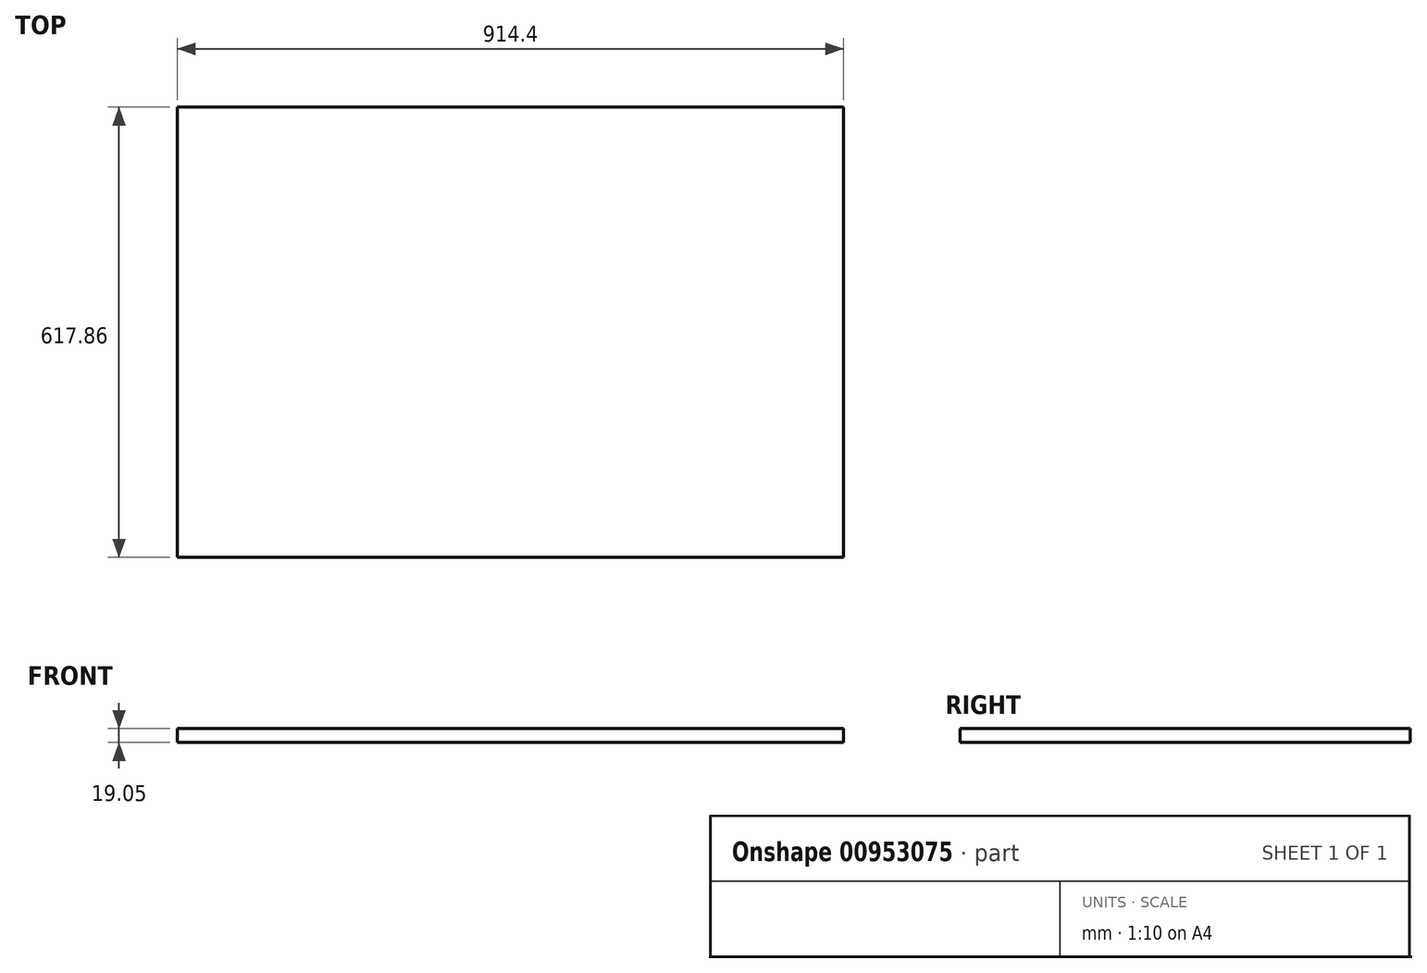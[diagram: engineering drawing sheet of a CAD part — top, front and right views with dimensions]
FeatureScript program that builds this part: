
annotation { "Feature Type Name" : "Feature", "Feature Type Description" : "" }
export const myFeature = defineFeature(function(context is Context, id is Id, definition is map)
    precondition{}
    {
        {
            var Q0;
            Q0=qCreatedBy(makeId("Top.planeOp"),FACE);
            var sketch = newSketch(context, id + "F0", { "sketchPlane" : qUnion([Q0])});
            skLineSegment(sketch, "E0", {"start": v(0, 0) * mm, "end": v(-914.4, 0) * mm});
            skLineSegment(sketch, "E1", {"start": v(-914.4, 0) * mm, "end": v(-914.4, 617.85) * mm});
            skLineSegment(sketch, "E2", {"start": v(-914.4, 617.85) * mm, "end": v(0, 617.85) * mm});
            skLineSegment(sketch, "E3", {"start": v(0, 617.85) * mm, "end": v(0, 0) * mm});
            skSolve(sketch);
        }
        {
            var Q0;
            Q0 = qSketchRegion(id + "F0", true);
            extrude(context, id + "F1", {"entities" : qUnion([Q0]), "depth" : 19.05 * mm, "offsetDistance" : 25.4 * mm});
        }
    });
